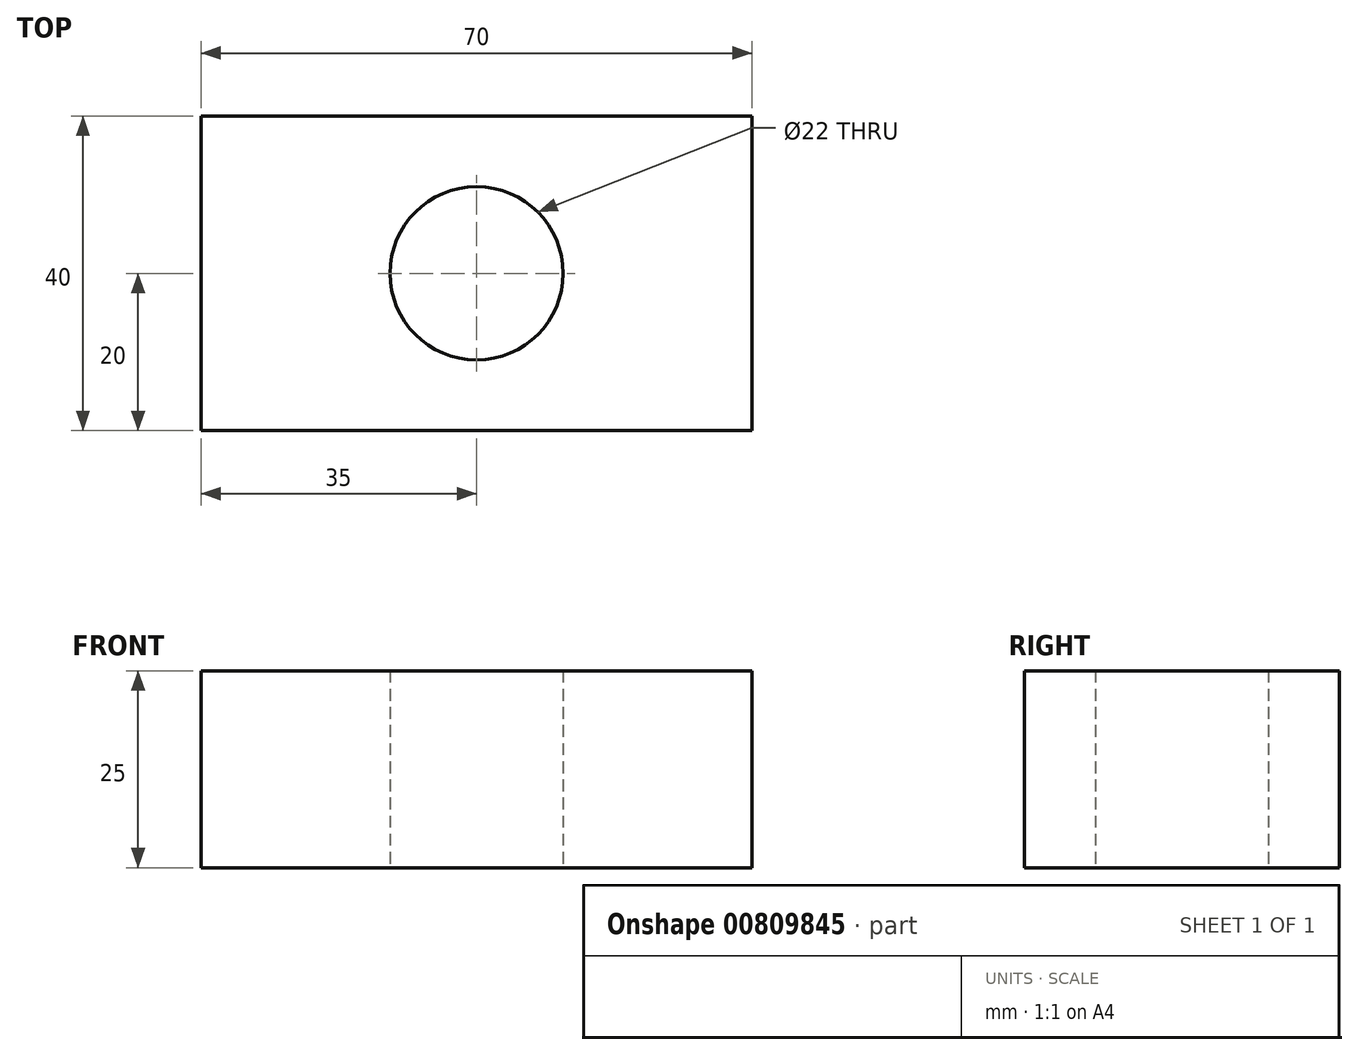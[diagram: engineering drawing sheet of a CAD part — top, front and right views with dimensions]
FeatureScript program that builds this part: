
annotation { "Feature Type Name" : "Feature", "Feature Type Description" : "" }
export const myFeature = defineFeature(function(context is Context, id is Id, definition is map)
    precondition{}
    {
        {
            var Q0;
            Q0=qCreatedBy(makeId("Top.planeOp"),FACE);
            var sketch = newSketch(context, id + "F0", { "sketchPlane" : qUnion([Q0])});
            skCircle(sketch, "E0", {"center": v(0, 0) * mm, "radius": 11 * mm});
            skLineSegment(sketch, "E1", {"start": v(0, -20) * mm, "end": v(-35, -20) * mm});
            skLineSegment(sketch, "E2", {"start": v(-35, -20) * mm, "end": v(-35, 20) * mm});
            skLineSegment(sketch, "E3", {"start": v(-35, 20) * mm, "end": v(0, 20) * mm});
            skLineSegment(sketch, "E4", {"start": v(0, 20) * mm, "end": v(35, 20) * mm});
            skLineSegment(sketch, "E5", {"start": v(35, 20) * mm, "end": v(35, -20) * mm});
            skLineSegment(sketch, "E6", {"start": v(35, -20) * mm, "end": v(0, -20) * mm});
            skSolve(sketch);
        }
        {
            var Q0;
            Q0=makeQuery(id+"F0.imprint","IMPRINT",FACE,{"disambiguationData":[TD([[makeQuery(id+"F0.imprint","IMPRINT",EDGE,{"derivedFrom":sQuery(id+"F0.wireOp",EDGE,"E0")}),-1.0]])]});
            extrude(context, id + "F1", {"entities" : qUnion([Q0]), "depth" : 25 * mm, "offsetDistance" : 25 * mm});
        }
    });
